# Revit family: Shower-Shower_Door-KOHLER-Fluence-K-702208_1
name_source: partatom
category: Specialty Equipment
units: mm (PartAtom-declared; Revit-internal decimal feet)

## family parameters
Cut with Voids When Loaded = No
Host = Face
OmniClass Number = 23.31.17.17
OmniClass Title = Shower Enclosures
Part Type = Normal
Room Calculation Point = No
Round Connector Dimension = Use Diameter
Shared = No

## types (6) — shared parameters
ADA Compliant = No
Assembly Code = C1030200
Date Modified = 08/15/2022
Default Elevation = 4"
Hardware Included = Yes
Height = 70"
Length = 7 1/4"
Manufacturer = Kohler Co.
Master Format 2014 = 10 28 19.16
Master Format 2014 Name = Shower Doors
Material = Premium Metal Construction
Product Documentation Link = https://www.us.kohler.com
Product Name = Fluence
Product Page URL = https://www.us.kohler.com
URL = https://www.us.kohler.com
WaterSense Certified = No

## per-type parameters (varying)
| type | Description | Finish | Model | Secondary Finish | Type |
| Clear Glass,ABV-Anodized Brushed Bronze | 44-5/8 - 47-5/8  Inch W x 70-9/32 Inch H sliding shower door with 1/4 Inch thick Crystal Clear glass | Kohler-Metal-ABV-Anodized_Brushed_Bronze | K-702208-6L-ABV | Kohler-Glass-L-Crystal_Clear | 1 |
| Clear Glass,MX-Matte Nickel | 44-5/8 - 47-5/8  Inch W x 70-9/32 Inch H sliding shower door with 1/4 Inch thick Crystal Clear glass | Kohler-Metal-MX-Matte_Nickel | K-702208-6L-MX | Kohler-Glass-L-Crystal_Clear | 2 |
| Clear Glass,SHP-Bright Polished Silver | 44-5/8 - 47-5/8  Inch W x 70-9/32 Inch H sliding shower door with 1/4 Inch thick Crystal Clear glass | Kohler-Metal-SHP-Bright_Polished_Silver | K-702208-6L-SHP | Kohler-Glass-L-Crystal_Clear | 3 |
| Falling Lines Glass,ABV-Anodized Brushed Bronze | 44-5/8 - 47-5/8 Inch W x 70-9/32 Inch H sliding shower door with 1/4 Inch thick Falling Lines glass | Kohler-Metal-ABV-Anodized_Brushed_Bronze | K-702208-6G54-ABV | KOHLER-Glass-G54-Falling_Lines | 4 |
| Falling Lines Glass,MX-Matte Nickel | 44-5/8 - 47-5/8 Inch W x 70-9/32 Inch H sliding shower door with 1/4 Inch thick Falling Lines glass | Kohler-Metal-MX-Matte_Nickel | K-702208-6G54-MX | KOHLER-Glass-G54-Falling_Lines | 5 |
| Falling Lines Glass,SHP-Bright Polished Silver | 44-5/8 - 47-5/8 Inch W x 70-9/32 Inch H sliding shower door with 1/4 Inch thick Falling Lines glass | Kohler-Metal-SHP-Bright_Polished_Silver | K-702208-6G54-SHP | KOHLER-Glass-G54-Falling_Lines | 6 |

## geometry (parser evidence)
native form markers: Sweep x4
no freeform markers — native parametric forms only
